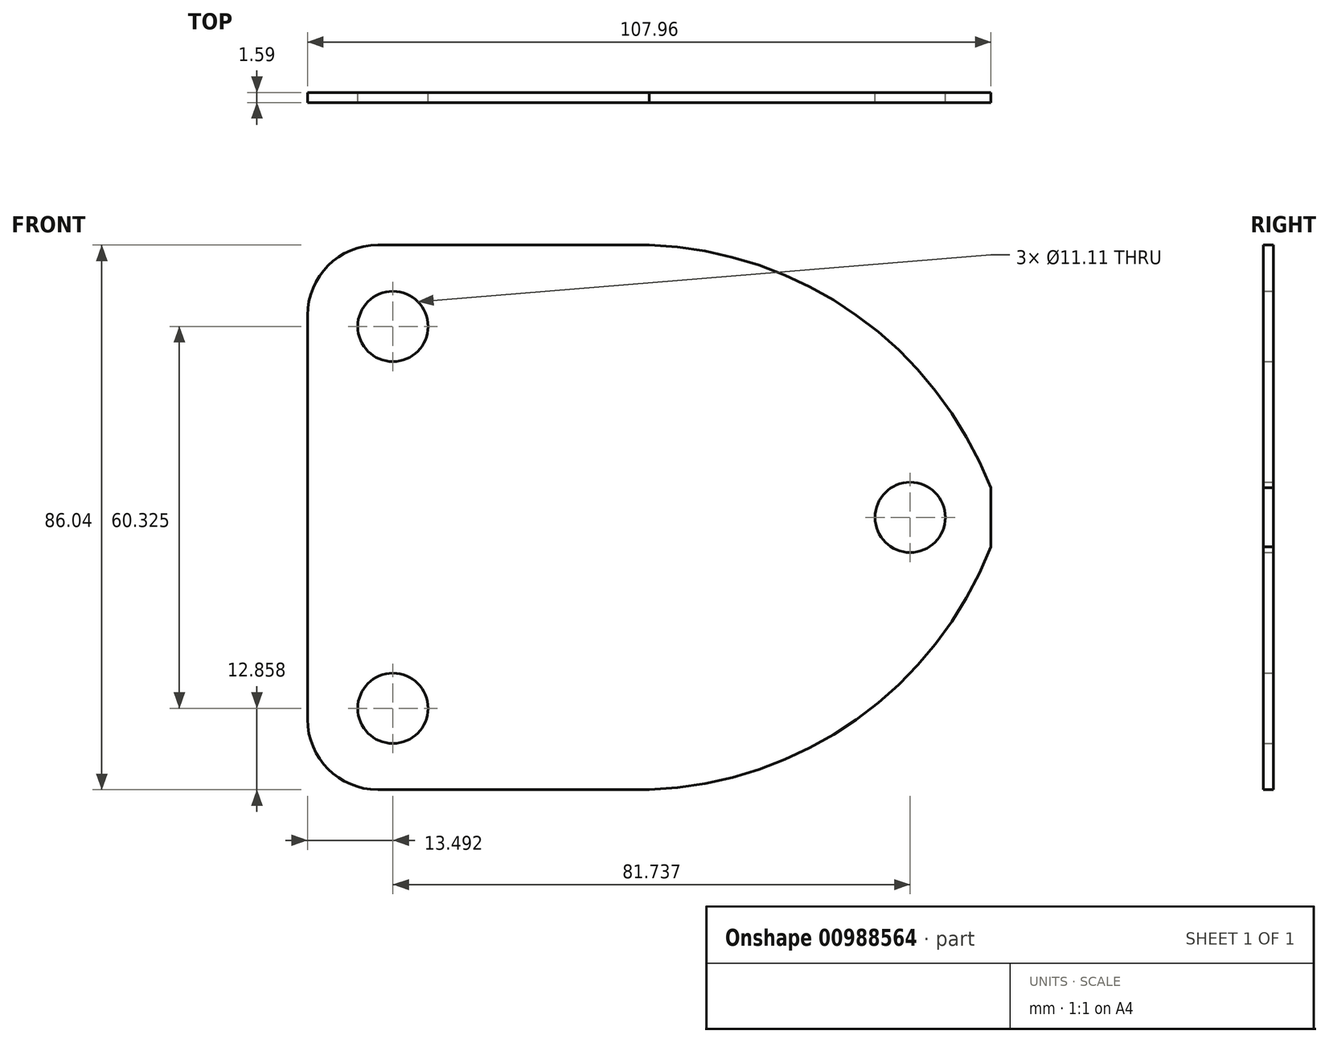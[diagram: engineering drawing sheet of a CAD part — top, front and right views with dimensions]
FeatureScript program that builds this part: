
annotation { "Feature Type Name" : "Feature", "Feature Type Description" : "" }
export const myFeature = defineFeature(function(context is Context, id is Id, definition is map)
    precondition{}
    {
        {
            var Q0;
            Q0=qCreatedBy(makeId("Front.planeOp"),FACE);
            var sketch = newSketch(context, id + "F0", { "sketchPlane" : qUnion([Q0])});
            skLineSegment(sketch, "E0.bottom", {"start": v(53.97, -43.02) * mm, "end": v(-53.98, -43.02) * mm});
            skLineSegment(sketch, "E0.top", {"start": v(53.98, 43.02) * mm, "end": v(-53.97, 43.02) * mm});
            skLineSegment(sketch, "E0.left", {"start": v(53.97, -43.02) * mm, "end": v(53.98, 43.02) * mm});
            skLineSegment(sketch, "E0.right", {"start": v(-53.98, -43.02) * mm, "end": v(-53.97, 43.02) * mm});
            skPoint(sketch, "E0.middle", {"position": v(0, 0) * mm});
            skSolve(sketch);
        }
        {
            var Q0;
            Q0=qSketchRegion(id+"F0",true);
            extrude(context, id + "F1", {"entities" : qUnion([Q0]), "depth" : 1.59 * mm, "offsetDistance" : 25.4 * mm});
        }
        {
            var Q0;
            Q0=makeQuery(id+"F1.opExtrude","SWEPT_EDGE",EDGE,{"disambiguationData":[OSD([sQuery(id+"F0.wireOp",EDGE,"E0.top"),sQuery(id+"F0.wireOp",EDGE,"E0.right")])]});
            var Q1;
            Q1=makeQuery(id+"F1.opExtrude","SWEPT_EDGE",EDGE,{"disambiguationData":[OSD([sQuery(id+"F0.wireOp",EDGE,"E0.bottom"),sQuery(id+"F0.wireOp",EDGE,"E0.right")])]});
            fillet(context, id + "F2", {"entities" : qUnion([Q0, Q1]), "radius" : 11.1 * mm, "tangentPropagation" : true, "allowEdgeOverflow" : false});
        }
        {
            var Q0;
            Q0=qCreatedBy(makeId("Front.planeOp"),FACE);
            var sketch = newSketch(context, id + "F3", { "sketchPlane" : qUnion([Q0])});
            skCircle(sketch, "E1", {"center": v(-40.49, 30.16) * mm, "radius": 5.56 * mm});
            skCircle(sketch, "E2", {"center": v(-40.49, -30.16) * mm, "radius": 5.56 * mm});
            skCircle(sketch, "E3", {"center": v(41.25, 0) * mm, "radius": 5.56 * mm});
            skLineSegment(sketch, "E4", {"start": v(-40.49, -30.16) * mm, "end": v(-40.49, 0) * mm, "construction": true});
            skLineSegment(sketch, "E5", {"start": v(-40.49, 0) * mm, "end": v(-40.49, 30.16) * mm, "construction": true});
            skSolve(sketch);
        }
        {
            var Q0;
            Q0=qSketchRegion(id+"F3",true);
            extrude(context, id + "F4", {"entities" : qUnion([Q0]), "operationType" : NewBodyOperationType.REMOVE, "endBound" : BoundingType.THROUGH_ALL, "depth" : 25.4 * mm, "offsetDistance" : 25.4 * mm});
        }
        {
            var Q0;
            Q0=qCreatedBy(makeId("Front.planeOp"),FACE);
            var sketch = newSketch(context, id + "F5", { "sketchPlane" : qUnion([Q0])});
            skLineSegment(sketch, "E6", {"start": v(0, -43.02) * mm, "end": v(0, 43.02) * mm, "construction": true});
            skArc(sketch, "E7", {"start": v(55.56, 0) * mm, "mid": v(34.72, 30.47) * mm, "end": v(0, 43.02) * mm});
            skArc(sketch, "E8", {"start": v(0, -43.02) * mm, "mid": v(34.72, -30.47) * mm, "end": v(55.56, 0) * mm});
            skLineSegment(sketch, "E9", {"start": v(0, 43.02) * mm, "end": v(73.44, 43.02) * mm});
            skLineSegment(sketch, "E10", {"start": v(73.44, 43.02) * mm, "end": v(73.44, -43.02) * mm});
            skLineSegment(sketch, "E11", {"start": v(73.44, -43.02) * mm, "end": v(0, -43.02) * mm});
            skSolve(sketch);
        }
        {
            var Q0;
            Q0=qSketchRegion(id+"F5",true);
            extrude(context, id + "F6", {"entities" : qUnion([Q0]), "operationType" : NewBodyOperationType.REMOVE, "endBound" : BoundingType.THROUGH_ALL, "depth" : 25.4 * mm, "offsetDistance" : 25.4 * mm});
        }
    });
